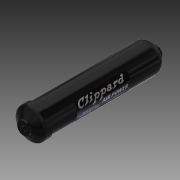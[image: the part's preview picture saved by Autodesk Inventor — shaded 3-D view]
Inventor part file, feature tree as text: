
AUTODESK INVENTOR PART (.ipt)
format: ipt  version: 2018 (Build 220112000, 112)  size: 184,320 bytes
history: native  units: in
note: dims shown in document units (in); Inventor stores cm internally (conversion verified against a paired STEP export)
features: sketch x8, extrude x4, revolve x3, fillet x2, other x2, projected_geometry x2, plane x1
ambient origin geometry x8: Origin, YZ Plane, XZ Plane, XY Plane, X Axis, Y Axis, Z Axis, Center Point
bodies: Solid1 (feature_tree)
feature tree (22):
  revolve  "Revolution1"  [1 undecoded]
  fillet  "Fillet1"  [1 undecoded]
  revolve  "Revolution2"  [1 undecoded]
  fillet  "Fillet2"  Radius=0.75in
  revolve  "Revolution3"  [1 undecoded]
  extrude  "Extrusion1"  Depth=0.144in TaperAngle=0.0deg
  extrude  "Extrusion2"  Depth=0.1in TaperAngle=0.0deg
  extrude  "Extrusion3"  [1 undecoded]
  extrude  "Extrusion4"  [1 undecoded]
  plane  "Work Plane1"
  other  "Decal1"
  sketch  "Sketch1"  dims[d0=1.28in d1=10.459in d2=90.0deg]
  sketch  "Sketch2"  dims[d3=0.75in d4=1.39in d5=0.75in]
  sketch  "Sketch3"  dims[d6=90.0deg d7=0.25in]
  sketch  "Sketch4"  dims[d8=90.0deg d9=0.144in d10=0.0in]
  projected_geometry  "Projected Loop1"
  sketch  "Sketch5"  dims[d11=0.322in d12=0.0in d13=0.1in d14=0.0in]
  projected_geometry  "Projected Loop2"
  sketch  "Sketch6"  dims[d15=0.1in d16=0.0in]
  sketch  "Sketch7"
  sketch  "Sketch8"
  other  "Image1"
note: 6 required parameter values undecoded (feature->parameter linkage not recoverable at this tier; creation-order binding heuristic only, values carry confidence <= 0.55)